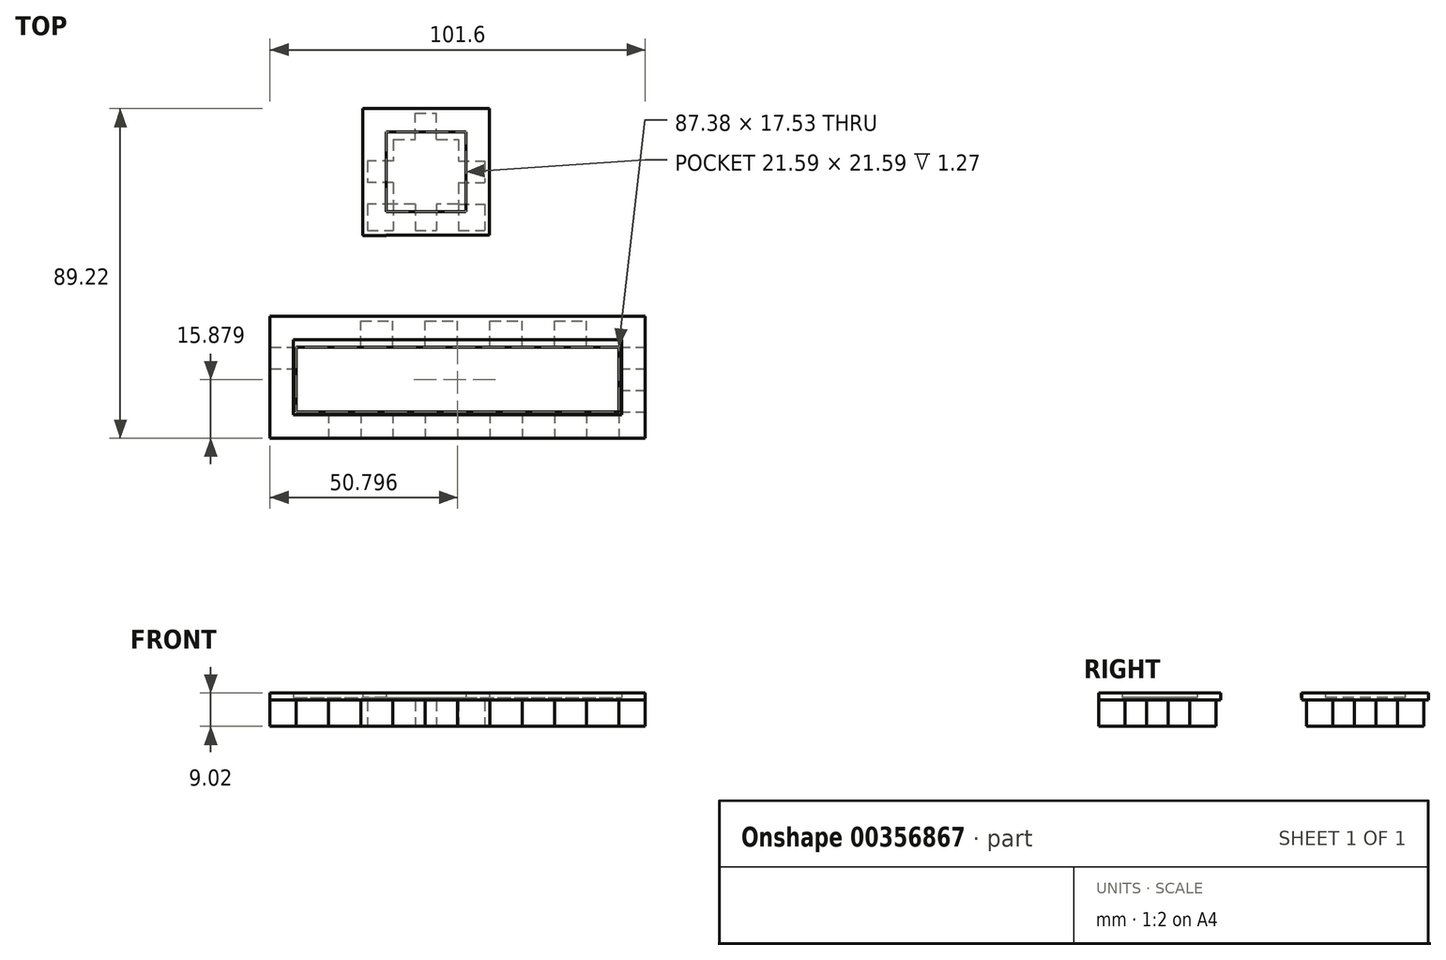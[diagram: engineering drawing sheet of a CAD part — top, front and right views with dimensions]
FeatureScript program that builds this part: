
annotation { "Feature Type Name" : "Feature", "Feature Type Description" : "" }
export const myFeature = defineFeature(function(context is Context, id is Id, definition is map)
    precondition{}
    {
        {
            var Q0;
            Q0=qCreatedBy(makeId("Top.planeOp"),FACE);
            var sketch = newSketch(context, id + "F0", { "sketchPlane" : qUnion([Q0])});
            skLineSegment(sketch, "E0.bottom", {"start": v(-52.12, 11.37) * mm, "end": v(49.48, 11.37) * mm});
            skLineSegment(sketch, "E0.top", {"start": v(-52.12, -20.38) * mm, "end": v(49.48, -20.38) * mm});
            skLineSegment(sketch, "E0.left", {"start": v(-52.12, 11.37) * mm, "end": v(-52.12, -20.38) * mm});
            skLineSegment(sketch, "E0.right", {"start": v(49.48, 11.37) * mm, "end": v(49.48, -20.38) * mm});
            skLineSegment(sketch, "E1.bottom", {"start": v(-52.12, 11.37) * mm, "end": v(-45.01, 11.37) * mm});
            skLineSegment(sketch, "E1.top", {"start": v(-52.12, 4.26) * mm, "end": v(-45.01, 4.26) * mm});
            skLineSegment(sketch, "E1.left", {"start": v(-52.12, 11.37) * mm, "end": v(-52.12, 4.26) * mm});
            skLineSegment(sketch, "E1.right", {"start": v(-45.01, 11.37) * mm, "end": v(-45.01, 4.26) * mm});
            skLineSegment(sketch, "E2.bottom", {"start": v(-45.01, 11.37) * mm, "end": v(-36.27, 11.37) * mm});
            skLineSegment(sketch, "E2.top", {"start": v(-45.01, 4.26) * mm, "end": v(-36.27, 4.26) * mm});
            skLineSegment(sketch, "E2.right", {"start": v(-36.27, 11.37) * mm, "end": v(-36.27, 4.26) * mm});
            skLineSegment(sketch, "E3.bottom", {"start": v(-36.27, 4.26) * mm, "end": v(-27.54, 4.26) * mm});
            skLineSegment(sketch, "E3.top", {"start": v(-36.27, 11.37) * mm, "end": v(-27.54, 11.37) * mm});
            skLineSegment(sketch, "E3.left", {"start": v(-36.27, 4.26) * mm, "end": v(-36.27, 11.37) * mm});
            skLineSegment(sketch, "E3.right", {"start": v(-27.54, 4.26) * mm, "end": v(-27.54, 11.37) * mm});
            skLineSegment(sketch, "E4.bottom", {"start": v(-27.54, 4.26) * mm, "end": v(-18.8, 4.26) * mm});
            skLineSegment(sketch, "E4.top", {"start": v(-27.54, 11.37) * mm, "end": v(-18.8, 11.37) * mm});
            skLineSegment(sketch, "E4.right", {"start": v(-18.8, 4.26) * mm, "end": v(-18.8, 11.37) * mm});
            skLineSegment(sketch, "E5.bottom", {"start": v(-18.8, 4.26) * mm, "end": v(-10.06, 4.26) * mm});
            skLineSegment(sketch, "E5.top", {"start": v(-18.8, 11.37) * mm, "end": v(-10.06, 11.37) * mm});
            skLineSegment(sketch, "E5.right", {"start": v(-10.06, 4.26) * mm, "end": v(-10.06, 11.37) * mm});
            skLineSegment(sketch, "E6.bottom", {"start": v(-10.06, 4.26) * mm, "end": v(-10.06, 4.26) * mm});
            skLineSegment(sketch, "E6.top", {"start": v(-10.06, 11.37) * mm, "end": v(-10.06, 11.37) * mm});
            skLineSegment(sketch, "E7.bottom", {"start": v(-10.06, 4.26) * mm, "end": v(-1.32, 4.26) * mm});
            skLineSegment(sketch, "E7.top", {"start": v(-10.06, 11.37) * mm, "end": v(-1.32, 11.37) * mm});
            skLineSegment(sketch, "E7.right", {"start": v(-1.32, 4.26) * mm, "end": v(-1.32, 11.37) * mm});
            skLineSegment(sketch, "E8.bottom", {"start": v(-1.32, 4.26) * mm, "end": v(7.41, 4.26) * mm});
            skLineSegment(sketch, "E8.top", {"start": v(-1.32, 11.37) * mm, "end": v(7.41, 11.37) * mm});
            skLineSegment(sketch, "E8.right", {"start": v(7.41, 4.26) * mm, "end": v(7.41, 11.37) * mm});
            skLineSegment(sketch, "E9.bottom", {"start": v(7.41, 4.26) * mm, "end": v(16.15, 4.26) * mm});
            skLineSegment(sketch, "E9.top", {"start": v(7.41, 11.37) * mm, "end": v(16.15, 11.37) * mm});
            skLineSegment(sketch, "E9.right", {"start": v(16.15, 4.26) * mm, "end": v(16.15, 11.37) * mm});
            skLineSegment(sketch, "E10.bottom", {"start": v(16.15, 4.26) * mm, "end": v(24.89, 4.26) * mm});
            skLineSegment(sketch, "E10.top", {"start": v(16.15, 11.37) * mm, "end": v(24.89, 11.37) * mm});
            skLineSegment(sketch, "E10.right", {"start": v(24.89, 4.26) * mm, "end": v(24.89, 11.37) * mm});
            skLineSegment(sketch, "E11.bottom", {"start": v(24.89, 4.26) * mm, "end": v(24.89, 4.26) * mm});
            skLineSegment(sketch, "E11.top", {"start": v(24.89, 11.37) * mm, "end": v(24.89, 11.37) * mm});
            skLineSegment(sketch, "E12.bottom", {"start": v(24.89, 4.26) * mm, "end": v(33.63, 4.26) * mm});
            skLineSegment(sketch, "E12.top", {"start": v(24.89, 11.37) * mm, "end": v(33.63, 11.37) * mm});
            skLineSegment(sketch, "E12.right", {"start": v(33.63, 4.26) * mm, "end": v(33.63, 11.37) * mm});
            skLineSegment(sketch, "E13.bottom", {"start": v(33.63, 4.26) * mm, "end": v(42.36, 4.26) * mm});
            skLineSegment(sketch, "E13.top", {"start": v(33.63, 11.37) * mm, "end": v(42.36, 11.37) * mm});
            skLineSegment(sketch, "E13.right", {"start": v(42.36, 4.26) * mm, "end": v(42.36, 11.37) * mm});
            skLineSegment(sketch, "E14.bottom", {"start": v(42.36, 4.26) * mm, "end": v(49.48, 4.26) * mm});
            skLineSegment(sketch, "E14.top", {"start": v(42.36, 11.37) * mm, "end": v(49.48, 11.37) * mm});
            skLineSegment(sketch, "E14.right", {"start": v(49.48, 4.26) * mm, "end": v(49.48, 11.37) * mm});
            skLineSegment(sketch, "E15.bottom", {"start": v(-52.12, -20.38) * mm, "end": v(-45.01, -20.38) * mm});
            skLineSegment(sketch, "E15.top", {"start": v(-52.12, -13.26) * mm, "end": v(-45.01, -13.26) * mm});
            skLineSegment(sketch, "E15.left", {"start": v(-52.12, -20.38) * mm, "end": v(-52.12, -13.26) * mm});
            skLineSegment(sketch, "E15.right", {"start": v(-45.01, -20.38) * mm, "end": v(-45.01, -13.26) * mm});
            skLineSegment(sketch, "E16.bottom", {"start": v(-45.01, -13.26) * mm, "end": v(-45.01, -13.26) * mm});
            skLineSegment(sketch, "E16.top", {"start": v(-45.01, -20.38) * mm, "end": v(-45.01, -20.38) * mm});
            skLineSegment(sketch, "E16.left", {"start": v(-45.01, -13.26) * mm, "end": v(-45.01, -20.38) * mm});
            skLineSegment(sketch, "E16.right", {"start": v(-45.01, -13.26) * mm, "end": v(-45.01, -20.38) * mm});
            skLineSegment(sketch, "E17.bottom", {"start": v(-45.01, -13.26) * mm, "end": v(-36.27, -13.26) * mm});
            skLineSegment(sketch, "E17.top", {"start": v(-45.01, -20.38) * mm, "end": v(-36.27, -20.38) * mm});
            skLineSegment(sketch, "E17.right", {"start": v(-36.27, -13.26) * mm, "end": v(-36.27, -20.38) * mm});
            skLineSegment(sketch, "E18.bottom", {"start": v(-36.27, -13.26) * mm, "end": v(-36.27, -13.26) * mm});
            skLineSegment(sketch, "E18.top", {"start": v(-36.27, -20.38) * mm, "end": v(-36.27, -20.38) * mm});
            skLineSegment(sketch, "E19.bottom", {"start": v(-36.27, -13.26) * mm, "end": v(-27.54, -13.26) * mm});
            skLineSegment(sketch, "E19.top", {"start": v(-36.27, -20.38) * mm, "end": v(-27.54, -20.38) * mm});
            skLineSegment(sketch, "E19.right", {"start": v(-27.54, -13.26) * mm, "end": v(-27.54, -20.38) * mm});
            skLineSegment(sketch, "E20.bottom", {"start": v(-27.54, -13.26) * mm, "end": v(-18.8, -13.26) * mm});
            skLineSegment(sketch, "E20.top", {"start": v(-27.54, -20.38) * mm, "end": v(-18.8, -20.38) * mm});
            skLineSegment(sketch, "E20.right", {"start": v(-18.8, -13.26) * mm, "end": v(-18.8, -20.38) * mm});
            skLineSegment(sketch, "E21.bottom", {"start": v(-18.8, -13.26) * mm, "end": v(-10.06, -13.26) * mm});
            skLineSegment(sketch, "E21.top", {"start": v(-18.8, -20.38) * mm, "end": v(-10.06, -20.38) * mm});
            skLineSegment(sketch, "E21.right", {"start": v(-10.06, -13.26) * mm, "end": v(-10.06, -20.38) * mm});
            skLineSegment(sketch, "E22.bottom", {"start": v(-10.06, -13.26) * mm, "end": v(-1.32, -13.26) * mm});
            skLineSegment(sketch, "E22.top", {"start": v(-10.06, -20.38) * mm, "end": v(-1.32, -20.38) * mm});
            skLineSegment(sketch, "E22.right", {"start": v(-1.32, -13.26) * mm, "end": v(-1.32, -20.38) * mm});
            skLineSegment(sketch, "E23.bottom", {"start": v(-1.32, -13.26) * mm, "end": v(7.41, -13.26) * mm});
            skLineSegment(sketch, "E23.top", {"start": v(-1.32, -20.38) * mm, "end": v(7.41, -20.38) * mm});
            skLineSegment(sketch, "E23.right", {"start": v(7.41, -13.26) * mm, "end": v(7.41, -20.38) * mm});
            skLineSegment(sketch, "E24.bottom", {"start": v(7.41, -13.26) * mm, "end": v(16.15, -13.26) * mm});
            skLineSegment(sketch, "E24.top", {"start": v(7.41, -20.38) * mm, "end": v(16.15, -20.38) * mm});
            skLineSegment(sketch, "E24.right", {"start": v(16.15, -13.26) * mm, "end": v(16.15, -20.38) * mm});
            skLineSegment(sketch, "E25.bottom", {"start": v(16.15, -13.26) * mm, "end": v(24.89, -13.26) * mm});
            skLineSegment(sketch, "E25.top", {"start": v(16.15, -20.38) * mm, "end": v(24.89, -20.38) * mm});
            skLineSegment(sketch, "E25.right", {"start": v(24.89, -13.26) * mm, "end": v(24.89, -20.38) * mm});
            skLineSegment(sketch, "E26.bottom", {"start": v(24.89, -13.26) * mm, "end": v(33.63, -13.26) * mm});
            skLineSegment(sketch, "E26.top", {"start": v(24.89, -20.38) * mm, "end": v(33.63, -20.38) * mm});
            skLineSegment(sketch, "E26.right", {"start": v(33.63, -13.26) * mm, "end": v(33.63, -20.38) * mm});
            skLineSegment(sketch, "E27.bottom", {"start": v(33.63, -13.26) * mm, "end": v(42.36, -13.26) * mm});
            skLineSegment(sketch, "E27.top", {"start": v(33.63, -20.38) * mm, "end": v(42.36, -20.38) * mm});
            skLineSegment(sketch, "E27.right", {"start": v(42.36, -13.26) * mm, "end": v(42.36, -20.38) * mm});
            skLineSegment(sketch, "E28.bottom", {"start": v(42.36, -13.26) * mm, "end": v(49.48, -13.26) * mm});
            skLineSegment(sketch, "E28.top", {"start": v(42.36, -20.38) * mm, "end": v(49.48, -20.38) * mm});
            skLineSegment(sketch, "E28.right", {"start": v(49.48, -13.26) * mm, "end": v(49.48, -20.38) * mm});
            skLineSegment(sketch, "E29.top", {"start": v(-52.12, -1.58) * mm, "end": v(-45.01, -1.58) * mm});
            skLineSegment(sketch, "E29.left", {"start": v(-52.12, 4.26) * mm, "end": v(-52.12, -1.58) * mm});
            skLineSegment(sketch, "E29.right", {"start": v(-45.01, 4.26) * mm, "end": v(-45.01, -1.58) * mm});
            skLineSegment(sketch, "E30.top", {"start": v(-52.12, -7.42) * mm, "end": v(-45.01, -7.42) * mm});
            skLineSegment(sketch, "E30.left", {"start": v(-52.12, -1.58) * mm, "end": v(-52.12, -7.42) * mm});
            skLineSegment(sketch, "E30.right", {"start": v(-45.01, -1.58) * mm, "end": v(-45.01, -7.42) * mm});
            skLineSegment(sketch, "E31.bottom", {"start": v(-45.01, -7.42) * mm, "end": v(-52.12, -7.42) * mm});
            skLineSegment(sketch, "E31.top", {"start": v(-45.01, -13.26) * mm, "end": v(-52.12, -13.26) * mm});
            skLineSegment(sketch, "E31.left", {"start": v(-45.01, -7.42) * mm, "end": v(-45.01, -13.26) * mm});
            skLineSegment(sketch, "E31.right", {"start": v(-52.12, -7.42) * mm, "end": v(-52.12, -13.26) * mm});
            skLineSegment(sketch, "E32.top", {"start": v(42.36, -1.58) * mm, "end": v(49.48, -1.58) * mm});
            skLineSegment(sketch, "E32.left", {"start": v(42.36, 4.26) * mm, "end": v(42.36, -1.58) * mm});
            skLineSegment(sketch, "E32.right", {"start": v(49.48, 4.26) * mm, "end": v(49.48, -1.58) * mm});
            skLineSegment(sketch, "E33.top", {"start": v(42.36, -7.42) * mm, "end": v(49.48, -7.42) * mm});
            skLineSegment(sketch, "E33.left", {"start": v(42.36, -1.58) * mm, "end": v(42.36, -7.42) * mm});
            skLineSegment(sketch, "E33.right", {"start": v(49.48, -1.58) * mm, "end": v(49.48, -7.42) * mm});
            skLineSegment(sketch, "E34.left", {"start": v(42.36, -7.42) * mm, "end": v(42.36, -13.26) * mm});
            skLineSegment(sketch, "E34.right", {"start": v(49.48, -7.42) * mm, "end": v(49.48, -13.26) * mm});
            skSolve(sketch);
        }
        {
            var Q0;
            Q0=makeQuery(id+"F0.imprint","IMPRINT",FACE,{"disambiguationData":[TD([[makeQuery(id+"F0.imprint","IMPRINT",EDGE,{"derivedFrom":sQuery(id+"F0.wireOp",EDGE,"E2.top")}),-1.0]])]});
            var Q1;
            Q1=makeQuery(id+"F0.imprint","IMPRINT",FACE,{"disambiguationData":[TD([[makeQuery(id+"F0.imprint","IMPRINT",EDGE,{"derivedFrom":sQuery(id+"F0.wireOp",EDGE,"E2.bottom")}),-1.0]])]});
            var Q2;
            Q2=makeQuery(id+"F0.imprint","IMPRINT",FACE,{"disambiguationData":[TD([[makeQuery(id+"F0.imprint","IMPRINT",EDGE,{"derivedFrom":sQuery(id+"F0.wireOp",EDGE,"E4.bottom")}),1.0]])]});
            var Q3;
            Q3=makeQuery(id+"F0.imprint","IMPRINT",FACE,{"disambiguationData":[TD([[makeQuery(id+"F0.imprint","IMPRINT",EDGE,{"derivedFrom":sQuery(id+"F0.wireOp",EDGE,"E7.bottom")}),1.0]])]});
            var Q4;
            Q4=makeQuery(id+"F0.imprint","IMPRINT",FACE,{"disambiguationData":[TD([[makeQuery(id+"F0.imprint","IMPRINT",EDGE,{"derivedFrom":sQuery(id+"F0.wireOp",EDGE,"E9.bottom")}),1.0]])]});
            var Q5;
            Q5=makeQuery(id+"F0.imprint","IMPRINT",FACE,{"disambiguationData":[TD([[makeQuery(id+"F0.imprint","IMPRINT",EDGE,{"derivedFrom":sQuery(id+"F0.wireOp",EDGE,"E12.bottom")}),1.0]])]});
            var Q6;
            Q6=makeQuery(id+"F0.imprint","IMPRINT",FACE,{"disambiguationData":[TD([[makeQuery(id+"F0.imprint","IMPRINT",EDGE,{"derivedFrom":sQuery(id+"F0.wireOp",EDGE,"E14.bottom")}),-1.0]])]});
            var Q7;
            Q7=makeQuery(id+"F0.imprint","IMPRINT",FACE,{"disambiguationData":[TD([[makeQuery(id+"F0.imprint","IMPRINT",EDGE,{"derivedFrom":sQuery(id+"F0.wireOp",EDGE,"E33.top")}),-1.0]])]});
            var Q8;
            Q8=makeQuery(id+"F0.imprint","IMPRINT",FACE,{"disambiguationData":[TD([[makeQuery(id+"F0.imprint","IMPRINT",EDGE,{"derivedFrom":sQuery(id+"F0.wireOp",EDGE,"E27.bottom")}),-1.0]])]});
            var Q9;
            Q9=makeQuery(id+"F0.imprint","IMPRINT",FACE,{"disambiguationData":[TD([[makeQuery(id+"F0.imprint","IMPRINT",EDGE,{"derivedFrom":sQuery(id+"F0.wireOp",EDGE,"E25.bottom")}),-1.0]])]});
            var Q10;
            Q10=makeQuery(id+"F0.imprint","IMPRINT",FACE,{"disambiguationData":[TD([[makeQuery(id+"F0.imprint","IMPRINT",EDGE,{"derivedFrom":sQuery(id+"F0.wireOp",EDGE,"E23.bottom")}),-1.0]])]});
            var Q11;
            Q11=makeQuery(id+"F0.imprint","IMPRINT",FACE,{"disambiguationData":[TD([[makeQuery(id+"F0.imprint","IMPRINT",EDGE,{"derivedFrom":sQuery(id+"F0.wireOp",EDGE,"E21.bottom")}),-1.0]])]});
            var Q12;
            Q12=makeQuery(id+"F0.imprint","IMPRINT",FACE,{"disambiguationData":[TD([[makeQuery(id+"F0.imprint","IMPRINT",EDGE,{"derivedFrom":sQuery(id+"F0.wireOp",EDGE,"E19.bottom")}),-1.0]])]});
            var Q13;
            Q13=makeQuery(id+"F0.imprint","IMPRINT",FACE,{"disambiguationData":[TD([[makeQuery(id+"F0.imprint","IMPRINT",EDGE,{"derivedFrom":sQuery(id+"F0.wireOp",EDGE,"E31.bottom")}),1.0]])]});
            var Q14;
            Q14=makeQuery(id+"F0.imprint","IMPRINT",FACE,{"disambiguationData":[TD([[makeQuery(id+"F0.imprint","IMPRINT",EDGE,{"derivedFrom":sQuery(id+"F0.wireOp",EDGE,"E1.top")}),-1.0]])]});
            extrude(context, id + "F1", {"entities" : qUnion([Q0, Q1, Q2, Q3, Q4, Q5, Q6, Q7, Q8, Q9, Q10, Q11, Q12, Q13, Q14]), "depth" : 7.11 * mm});
        }
        {
            var Q0;
            Q0=makeQuery(id+"F1.opExtrude","CAP_FACE",FACE,{"disambiguationData":[OSD([sQuery(id+"F0.wireOp",EDGE,"E2.bottom"),sQuery(id+"F0.wireOp",EDGE,"E1.right"),sQuery(id+"F0.wireOp",EDGE,"E3.bottom"),sQuery(id+"F0.wireOp",EDGE,"E3.left"),sQuery(id+"F0.wireOp",EDGE,"E4.top"),sQuery(id+"F0.wireOp",EDGE,"E3.right"),sQuery(id+"F0.wireOp",EDGE,"E5.bottom"),sQuery(id+"F0.wireOp",EDGE,"E4.right"),sQuery(id+"F0.wireOp",EDGE,"E6.top"),sQuery(id+"F0.wireOp",EDGE,"E5.right"),sQuery(id+"F0.wireOp",EDGE,"E7.bottom"),sQuery(id+"F0.wireOp",EDGE,"E5.right"),sQuery(id+"F0.wireOp",EDGE,"E8.top"),sQuery(id+"F0.wireOp",EDGE,"E7.right"),sQuery(id+"F0.wireOp",EDGE,"E9.bottom"),sQuery(id+"F0.wireOp",EDGE,"E8.right"),sQuery(id+"F0.wireOp",EDGE,"E10.top"),sQuery(id+"F0.wireOp",EDGE,"E9.right"),sQuery(id+"F0.wireOp",EDGE,"E11.bottom"),sQuery(id+"F0.wireOp",EDGE,"E10.right"),sQuery(id+"F0.wireOp",EDGE,"E12.top"),sQuery(id+"F0.wireOp",EDGE,"E10.right"),sQuery(id+"F0.wireOp",EDGE,"E13.bottom"),sQuery(id+"F0.wireOp",EDGE,"E12.right"),sQuery(id+"F0.wireOp",EDGE,"E16.bottom"),sQuery(id+"F0.wireOp",EDGE,"E17.top"),sQuery(id+"F0.wireOp",EDGE,"E16.left"),sQuery(id+"F0.wireOp",EDGE,"E18.bottom"),sQuery(id+"F0.wireOp",EDGE,"E17.right"),sQuery(id+"F0.wireOp",EDGE,"E19.top"),sQuery(id+"F0.wireOp",EDGE,"E17.right"),sQuery(id+"F0.wireOp",EDGE,"E20.bottom"),sQuery(id+"F0.wireOp",EDGE,"E19.right"),sQuery(id+"F0.wireOp",EDGE,"E21.top"),sQuery(id+"F0.wireOp",EDGE,"E20.right"),sQuery(id+"F0.wireOp",EDGE,"E22.bottom"),sQuery(id+"F0.wireOp",EDGE,"E21.right"),sQuery(id+"F0.wireOp",EDGE,"E23.top"),sQuery(id+"F0.wireOp",EDGE,"E22.right"),sQuery(id+"F0.wireOp",EDGE,"E24.bottom"),sQuery(id+"F0.wireOp",EDGE,"E23.right"),sQuery(id+"F0.wireOp",EDGE,"E25.top"),sQuery(id+"F0.wireOp",EDGE,"E24.right"),sQuery(id+"F0.wireOp",EDGE,"E26.bottom"),sQuery(id+"F0.wireOp",EDGE,"E25.right"),sQuery(id+"F0.wireOp",EDGE,"E27.top"),sQuery(id+"F0.wireOp",EDGE,"E26.right"),sQuery(id+"F0.wireOp",EDGE,"E27.right"),sQuery(id+"F0.wireOp",EDGE,"E1.top"),sQuery(id+"F0.wireOp",EDGE,"E29.left"),sQuery(id+"F0.wireOp",EDGE,"E29.top"),sQuery(id+"F0.wireOp",EDGE,"E30.right"),sQuery(id+"F0.wireOp",EDGE,"E31.bottom"),sQuery(id+"F0.wireOp",EDGE,"E31.top"),sQuery(id+"F0.wireOp",EDGE,"E31.right"),sQuery(id+"F0.wireOp",EDGE,"E14.bottom"),sQuery(id+"F0.wireOp",EDGE,"E32.right"),sQuery(id+"F0.wireOp",EDGE,"E32.top"),sQuery(id+"F0.wireOp",EDGE,"E33.left"),sQuery(id+"F0.wireOp",EDGE,"E33.top"),sQuery(id+"F0.wireOp",EDGE,"E28.bottom"),sQuery(id+"F0.wireOp",EDGE,"E34.right")])],"isStart":false});
            var sketch = newSketch(context, id + "F2", { "sketchPlane" : qUnion([Q0])});
            skLineSegment(sketch, "E35.bottom", {"start": v(-52.12, -20.38) * mm, "end": v(-45.01, -20.38) * mm});
            skLineSegment(sketch, "E35.top", {"start": v(-52.12, 12.64) * mm, "end": v(-45.01, 12.64) * mm});
            skLineSegment(sketch, "E35.left", {"start": v(-52.12, -20.38) * mm, "end": v(-52.12, 12.64) * mm});
            skLineSegment(sketch, "E35.right", {"start": v(-45.01, -20.38) * mm, "end": v(-45.01, 12.64) * mm});
            skLineSegment(sketch, "E36.bottom", {"start": v(-52.12, -20.38) * mm, "end": v(49.48, -20.38) * mm});
            skLineSegment(sketch, "E36.top", {"start": v(-52.12, -13.26) * mm, "end": v(49.48, -13.26) * mm});
            skLineSegment(sketch, "E36.left", {"start": v(-52.12, -20.38) * mm, "end": v(-52.12, -13.26) * mm});
            skLineSegment(sketch, "E36.right", {"start": v(49.48, -20.38) * mm, "end": v(49.48, -13.26) * mm});
            skPoint(sketch, "E37.oppositeSnap0", {"position": v(42.36, -4.5) * mm});
            skLineSegment(sketch, "E37.bottom", {"start": v(49.48, -20.38) * mm, "end": v(42.36, -20.38) * mm});
            skLineSegment(sketch, "E37.top", {"start": v(49.48, 12.64) * mm, "end": v(42.36, 12.64) * mm});
            skLineSegment(sketch, "E37.left", {"start": v(49.48, -20.38) * mm, "end": v(49.48, 12.64) * mm});
            skLineSegment(sketch, "E37.right", {"start": v(42.36, -20.38) * mm, "end": v(42.36, 12.64) * mm});
            skLineSegment(sketch, "E38.bottom", {"start": v(-52.12, 12.64) * mm, "end": v(49.48, 12.64) * mm});
            skLineSegment(sketch, "E38.top", {"start": v(-52.12, 4.26) * mm, "end": v(49.48, 4.26) * mm});
            skLineSegment(sketch, "E38.left", {"start": v(-52.12, 12.64) * mm, "end": v(-52.12, 4.26) * mm});
            skLineSegment(sketch, "E38.right", {"start": v(49.48, 12.64) * mm, "end": v(49.48, 4.26) * mm});
            skSolve(sketch);
        }
        {
            var Q0;
            Q0 = qSketchRegion(id + "F2", true);
            var Q1;
            {var subQ5=sQuery(id+"F2.wireOp",EDGE,"E36.top");var subQ10=sQuery(id+"F2.wireOp",EDGE,"E35.right");var subQ12=makeQuery(id+"F2.imprint","INTERSECT",VERTEX,{"derivedFrom":[makeQuery(id+"F1.opExtrude","CAP_EDGE",EDGE,{"disambiguationData":[OSD([sQuery(id+"F0.wireOp",EDGE,"E31.bottom")])],"isStart":false}),subQ10]});var subQ24=makeQuery(id+"F2.imprint","INTERSECT",VERTEX,{"derivedFrom":[subQ10,subQ5]});Q1=makeQuery(id+"F2.imprint","IMPRINT",FACE,{"disambiguationData":[TD([[makeQuery(id+"F2.imprint","IMPRINT",EDGE,{"disambiguationData":[TD([[subQ12,1.0],[subQ24,-1.0]])],"derivedFrom":subQ10}),-1.0]])]});}
            extrude(context, id + "F3", {"entities" : qUnion([Q0, Q1]), "depth" : 0.64 * mm});
        }
        {
            var Q0;
            Q0=qCreatedBy(makeId("Top.planeOp"),FACE);
            var sketch = newSketch(context, id + "F4", { "sketchPlane" : qUnion([Q0])});
            skLineSegment(sketch, "E39.bottom", {"start": v(-25.78, 67.57) * mm, "end": v(5.97, 67.57) * mm});
            skLineSegment(sketch, "E39.top", {"start": v(-25.78, 35.82) * mm, "end": v(5.97, 35.82) * mm});
            skLineSegment(sketch, "E39.left", {"start": v(-25.78, 67.57) * mm, "end": v(-25.78, 35.82) * mm});
            skLineSegment(sketch, "E39.right", {"start": v(5.97, 67.57) * mm, "end": v(5.97, 35.82) * mm});
            skLineSegment(sketch, "E40.bottom", {"start": v(-25.78, 67.57) * mm, "end": v(-18.67, 67.57) * mm});
            skLineSegment(sketch, "E40.top", {"start": v(-25.78, 60.46) * mm, "end": v(-18.67, 60.46) * mm});
            skLineSegment(sketch, "E40.left", {"start": v(-25.78, 67.57) * mm, "end": v(-25.78, 60.46) * mm});
            skLineSegment(sketch, "E40.right", {"start": v(-18.67, 67.57) * mm, "end": v(-18.67, 60.46) * mm});
            skLineSegment(sketch, "E41.bottom", {"start": v(-18.67, 60.46) * mm, "end": v(-12.83, 60.46) * mm});
            skLineSegment(sketch, "E41.top", {"start": v(-18.67, 67.57) * mm, "end": v(-12.83, 67.57) * mm});
            skLineSegment(sketch, "E41.left", {"start": v(-18.67, 60.46) * mm, "end": v(-18.67, 67.57) * mm});
            skLineSegment(sketch, "E41.right", {"start": v(-12.83, 60.46) * mm, "end": v(-12.83, 67.57) * mm});
            skLineSegment(sketch, "E42.bottom", {"start": v(-12.83, 60.46) * mm, "end": v(-6.98, 60.46) * mm});
            skLineSegment(sketch, "E42.top", {"start": v(-12.83, 67.57) * mm, "end": v(-6.98, 67.57) * mm});
            skLineSegment(sketch, "E42.right", {"start": v(-6.98, 60.46) * mm, "end": v(-6.98, 67.57) * mm});
            skLineSegment(sketch, "E43.bottom", {"start": v(-6.98, 60.46) * mm, "end": v(-1.14, 60.46) * mm});
            skLineSegment(sketch, "E43.top", {"start": v(-6.98, 67.57) * mm, "end": v(-1.14, 67.57) * mm});
            skLineSegment(sketch, "E43.right", {"start": v(-1.14, 60.46) * mm, "end": v(-1.14, 67.57) * mm});
            skLineSegment(sketch, "E44.bottom", {"start": v(-1.14, 60.46) * mm, "end": v(5.97, 60.46) * mm});
            skLineSegment(sketch, "E44.top", {"start": v(-1.14, 67.57) * mm, "end": v(5.97, 67.57) * mm});
            skLineSegment(sketch, "E44.right", {"start": v(5.97, 60.46) * mm, "end": v(5.97, 67.57) * mm});
            skLineSegment(sketch, "E45.bottom", {"start": v(-18.67, 60.46) * mm, "end": v(-25.78, 60.46) * mm});
            skLineSegment(sketch, "E45.top", {"start": v(-18.67, 54.62) * mm, "end": v(-25.78, 54.62) * mm});
            skLineSegment(sketch, "E45.left", {"start": v(-18.67, 60.46) * mm, "end": v(-18.67, 54.62) * mm});
            skLineSegment(sketch, "E45.right", {"start": v(-25.78, 60.46) * mm, "end": v(-25.78, 54.62) * mm});
            skLineSegment(sketch, "E46.top", {"start": v(-18.67, 48.78) * mm, "end": v(-25.78, 48.78) * mm});
            skLineSegment(sketch, "E46.left", {"start": v(-18.67, 54.62) * mm, "end": v(-18.67, 48.78) * mm});
            skLineSegment(sketch, "E46.right", {"start": v(-25.78, 54.62) * mm, "end": v(-25.78, 48.78) * mm});
            skLineSegment(sketch, "E47.top", {"start": v(-18.67, 42.94) * mm, "end": v(-25.78, 42.94) * mm});
            skLineSegment(sketch, "E47.left", {"start": v(-18.67, 48.78) * mm, "end": v(-18.67, 42.94) * mm});
            skLineSegment(sketch, "E47.right", {"start": v(-25.78, 48.78) * mm, "end": v(-25.78, 42.94) * mm});
            skLineSegment(sketch, "E48.top", {"start": v(-18.67, 35.82) * mm, "end": v(-25.78, 35.82) * mm});
            skLineSegment(sketch, "E48.left", {"start": v(-18.67, 42.94) * mm, "end": v(-18.67, 35.82) * mm});
            skLineSegment(sketch, "E48.right", {"start": v(-25.78, 42.94) * mm, "end": v(-25.78, 35.82) * mm});
            skLineSegment(sketch, "E49.top", {"start": v(-1.14, 54.62) * mm, "end": v(5.97, 54.62) * mm});
            skLineSegment(sketch, "E49.left", {"start": v(-1.14, 60.46) * mm, "end": v(-1.14, 54.62) * mm});
            skLineSegment(sketch, "E49.right", {"start": v(5.97, 60.46) * mm, "end": v(5.97, 54.62) * mm});
            skLineSegment(sketch, "E50.top", {"start": v(-1.14, 48.78) * mm, "end": v(5.97, 48.78) * mm});
            skLineSegment(sketch, "E50.left", {"start": v(-1.14, 54.62) * mm, "end": v(-1.14, 48.78) * mm});
            skLineSegment(sketch, "E50.right", {"start": v(5.97, 54.62) * mm, "end": v(5.97, 48.78) * mm});
            skLineSegment(sketch, "E51.top", {"start": v(-1.14, 42.94) * mm, "end": v(5.97, 42.94) * mm});
            skLineSegment(sketch, "E51.left", {"start": v(-1.14, 48.78) * mm, "end": v(-1.14, 42.94) * mm});
            skLineSegment(sketch, "E51.right", {"start": v(5.97, 48.78) * mm, "end": v(5.97, 42.94) * mm});
            skLineSegment(sketch, "E52.top", {"start": v(-1.14, 35.82) * mm, "end": v(5.97, 35.82) * mm});
            skLineSegment(sketch, "E52.left", {"start": v(-1.14, 42.94) * mm, "end": v(-1.14, 35.82) * mm});
            skLineSegment(sketch, "E52.right", {"start": v(5.97, 42.94) * mm, "end": v(5.97, 35.82) * mm});
            skLineSegment(sketch, "E53.bottom", {"start": v(-1.14, 42.94) * mm, "end": v(-6.98, 42.94) * mm});
            skLineSegment(sketch, "E53.top", {"start": v(-1.14, 35.82) * mm, "end": v(-6.98, 35.82) * mm});
            skLineSegment(sketch, "E53.right", {"start": v(-6.98, 42.94) * mm, "end": v(-6.98, 35.82) * mm});
            skLineSegment(sketch, "E54.bottom", {"start": v(-6.98, 42.94) * mm, "end": v(-12.83, 42.94) * mm});
            skLineSegment(sketch, "E54.top", {"start": v(-6.98, 35.82) * mm, "end": v(-12.83, 35.82) * mm});
            skLineSegment(sketch, "E54.right", {"start": v(-12.83, 42.94) * mm, "end": v(-12.83, 35.82) * mm});
            skLineSegment(sketch, "E55.bottom", {"start": v(-12.83, 42.94) * mm, "end": v(-18.67, 42.94) * mm});
            skLineSegment(sketch, "E55.top", {"start": v(-12.83, 35.82) * mm, "end": v(-18.67, 35.82) * mm});
            skSolve(sketch);
        }
        {
            var Q0;
            Q0=makeQuery(id+"F4.imprint","IMPRINT",FACE,{"disambiguationData":[TD([[makeQuery(id+"F4.imprint","IMPRINT",EDGE,{"derivedFrom":sQuery(id+"F4.wireOp",EDGE,"E40.bottom")}),-1.0]])]});
            var Q1;
            Q1=makeQuery(id+"F4.imprint","IMPRINT",FACE,{"disambiguationData":[TD([[makeQuery(id+"F4.imprint","IMPRINT",EDGE,{"derivedFrom":sQuery(id+"F4.wireOp",EDGE,"E42.bottom")}),1.0]])]});
            var Q2;
            Q2=makeQuery(id+"F4.imprint","IMPRINT",FACE,{"disambiguationData":[TD([[makeQuery(id+"F4.imprint","IMPRINT",EDGE,{"derivedFrom":sQuery(id+"F4.wireOp",EDGE,"E41.bottom")}),-1.0]])]});
            var Q3;
            Q3=makeQuery(id+"F4.imprint","IMPRINT",FACE,{"disambiguationData":[TD([[makeQuery(id+"F4.imprint","IMPRINT",EDGE,{"derivedFrom":sQuery(id+"F4.wireOp",EDGE,"E44.top")}),-1.0]])]});
            var Q4;
            Q4=makeQuery(id+"F4.imprint","IMPRINT",FACE,{"disambiguationData":[TD([[makeQuery(id+"F4.imprint","IMPRINT",EDGE,{"derivedFrom":sQuery(id+"F4.wireOp",EDGE,"E49.top")}),-1.0]])]});
            var Q5;
            Q5=makeQuery(id+"F4.imprint","IMPRINT",FACE,{"disambiguationData":[TD([[makeQuery(id+"F4.imprint","IMPRINT",EDGE,{"derivedFrom":sQuery(id+"F4.wireOp",EDGE,"E51.top")}),-1.0]])]});
            var Q6;
            Q6=makeQuery(id+"F4.imprint","IMPRINT",FACE,{"disambiguationData":[TD([[makeQuery(id+"F4.imprint","IMPRINT",EDGE,{"derivedFrom":sQuery(id+"F4.wireOp",EDGE,"E54.bottom")}),1.0]])]});
            var Q7;
            Q7=makeQuery(id+"F4.imprint","IMPRINT",FACE,{"disambiguationData":[TD([[makeQuery(id+"F4.imprint","IMPRINT",EDGE,{"derivedFrom":sQuery(id+"F4.wireOp",EDGE,"E47.top")}),1.0]])]});
            var Q8;
            Q8=makeQuery(id+"F4.imprint","IMPRINT",FACE,{"disambiguationData":[TD([[makeQuery(id+"F4.imprint","IMPRINT",EDGE,{"derivedFrom":sQuery(id+"F4.wireOp",EDGE,"E45.top")}),1.0]])]});
            extrude(context, id + "F5", {"entities" : qUnion([Q0, Q1, Q2, Q3, Q4, Q5, Q6, Q7, Q8]), "depth" : 7.11 * mm});
        }
        {
            var Q0;
            Q0=makeQuery(id+"F5.opExtrude","CAP_FACE",FACE,{"disambiguationData":[OSD([sQuery(id+"F4.wireOp",EDGE,"E41.bottom"),sQuery(id+"F4.wireOp",EDGE,"E42.top"),sQuery(id+"F4.wireOp",EDGE,"E41.right"),sQuery(id+"F4.wireOp",EDGE,"E43.bottom"),sQuery(id+"F4.wireOp",EDGE,"E42.right"),sQuery(id+"F4.wireOp",EDGE,"E45.left"),sQuery(id+"F4.wireOp",EDGE,"E45.top"),sQuery(id+"F4.wireOp",EDGE,"E46.right"),sQuery(id+"F4.wireOp",EDGE,"E46.top"),sQuery(id+"F4.wireOp",EDGE,"E47.left"),sQuery(id+"F4.wireOp",EDGE,"E49.left"),sQuery(id+"F4.wireOp",EDGE,"E49.top"),sQuery(id+"F4.wireOp",EDGE,"E50.right"),sQuery(id+"F4.wireOp",EDGE,"E50.top"),sQuery(id+"F4.wireOp",EDGE,"E51.left"),sQuery(id+"F4.wireOp",EDGE,"E53.bottom"),sQuery(id+"F4.wireOp",EDGE,"E54.top"),sQuery(id+"F4.wireOp",EDGE,"E53.right"),sQuery(id+"F4.wireOp",EDGE,"E55.bottom"),sQuery(id+"F4.wireOp",EDGE,"E54.right")])],"isStart":false});
            var sketch = newSketch(context, id + "F6", { "sketchPlane" : qUnion([Q0])});
            skLineSegment(sketch, "E56.bottom", {"start": v(-18.67, 34.55) * mm, "end": v(-27.05, 34.55) * mm});
            skLineSegment(sketch, "E56.top", {"start": v(-18.67, 68.84) * mm, "end": v(-27.05, 68.84) * mm});
            skLineSegment(sketch, "E56.left", {"start": v(-18.67, 34.55) * mm, "end": v(-18.67, 68.84) * mm});
            skLineSegment(sketch, "E56.right", {"start": v(-27.05, 34.55) * mm, "end": v(-27.05, 68.84) * mm});
            skPoint(sketch, "E57.oppositeSnap0", {"position": v(-4.06, 60.46) * mm});
            skLineSegment(sketch, "E57.bottom", {"start": v(-27.05, 68.84) * mm, "end": v(7.24, 68.84) * mm});
            skLineSegment(sketch, "E57.top", {"start": v(-27.05, 60.46) * mm, "end": v(7.24, 60.46) * mm});
            skLineSegment(sketch, "E57.left", {"start": v(-27.05, 68.84) * mm, "end": v(-27.05, 60.46) * mm});
            skLineSegment(sketch, "E57.right", {"start": v(7.24, 68.84) * mm, "end": v(7.24, 60.46) * mm});
            skLineSegment(sketch, "E58.bottom", {"start": v(7.24, 68.84) * mm, "end": v(-1.14, 68.84) * mm});
            skLineSegment(sketch, "E58.top", {"start": v(7.24, 34.55) * mm, "end": v(-1.14, 34.55) * mm});
            skLineSegment(sketch, "E58.left", {"start": v(7.24, 68.84) * mm, "end": v(7.24, 34.55) * mm});
            skLineSegment(sketch, "E58.right", {"start": v(-1.14, 68.84) * mm, "end": v(-1.14, 34.55) * mm});
            skLineSegment(sketch, "E59.bottom", {"start": v(7.24, 34.55) * mm, "end": v(-27.05, 34.55) * mm});
            skLineSegment(sketch, "E59.top", {"start": v(7.24, 42.94) * mm, "end": v(-27.05, 42.94) * mm});
            skLineSegment(sketch, "E59.left", {"start": v(7.24, 34.55) * mm, "end": v(7.24, 42.94) * mm});
            skLineSegment(sketch, "E59.right", {"start": v(-27.05, 34.55) * mm, "end": v(-27.05, 42.94) * mm});
            skSolve(sketch);
        }
        {
            var Q0;
            Q0 = qSketchRegion(id + "F6", true);
            var Q1;
            {var subQ4=sQuery(id+"F6.wireOp",EDGE,"E56.left");var subQ5=makeQuery(id+"F6.imprint","INTERSECT",VERTEX,{"derivedFrom":[makeQuery(id+"F5.opExtrude","CAP_EDGE",EDGE,{"disambiguationData":[OSD([sQuery(id+"F4.wireOp",EDGE,"E46.top")])],"isStart":false}),subQ4]});var subQ13=makeQuery(id+"F6.imprint","INTERSECT",VERTEX,{"derivedFrom":[makeQuery(id+"F5.opExtrude","CAP_EDGE",EDGE,{"disambiguationData":[OSD([sQuery(id+"F4.wireOp",EDGE,"E45.top")])],"isStart":false}),subQ4]});Q1=makeQuery(id+"F6.imprint","IMPRINT",FACE,{"disambiguationData":[TD([[makeQuery(id+"F6.imprint","IMPRINT",EDGE,{"disambiguationData":[TD([[subQ13,1.0],[subQ5,-1.0]])],"derivedFrom":subQ4}),-1.0]])]});}
            extrude(context, id + "F7", {"entities" : qUnion([Q0, Q1]), "depth" : 0.64 * mm});
        }
        {
            var Q0;
            Q0=makeQuery(id+"F3.opExtrude","CAP_FACE",FACE,{"disambiguationData":[OSD([sQuery(id+"F2.wireOp",EDGE,"E35.left"),sQuery(id+"F2.wireOp",EDGE,"E36.bottom"),sQuery(id+"F2.wireOp",EDGE,"E36.left"),sQuery(id+"F2.wireOp",EDGE,"E37.bottom"),sQuery(id+"F2.wireOp",EDGE,"E37.left"),sQuery(id+"F2.wireOp",EDGE,"E38.bottom"),sQuery(id+"F2.wireOp",EDGE,"E38.left"),sQuery(id+"F2.wireOp",EDGE,"E38.right")])],"isStart":false});
            var sketch = newSketch(context, id + "F8", { "sketchPlane" : qUnion([Q0])});
            skLineSegment(sketch, "E60.bottom", {"start": v(-52.12, 12.64) * mm, "end": v(49.48, 12.64) * mm});
            skLineSegment(sketch, "E60.top", {"start": v(-52.12, 6.3) * mm, "end": v(49.48, 6.3) * mm});
            skLineSegment(sketch, "E60.left", {"start": v(-52.12, 12.64) * mm, "end": v(-52.12, 6.3) * mm});
            skLineSegment(sketch, "E60.right", {"start": v(49.48, 12.64) * mm, "end": v(49.48, 6.3) * mm});
            skLineSegment(sketch, "E61.bottom", {"start": v(-52.12, 12.64) * mm, "end": v(-45.77, 12.64) * mm});
            skLineSegment(sketch, "E61.top", {"start": v(-52.12, -20.38) * mm, "end": v(-45.77, -20.38) * mm});
            skLineSegment(sketch, "E61.left", {"start": v(-52.12, 12.64) * mm, "end": v(-52.12, -20.38) * mm});
            skLineSegment(sketch, "E61.right", {"start": v(-45.77, 12.64) * mm, "end": v(-45.77, -20.38) * mm});
            skLineSegment(sketch, "E62.bottom", {"start": v(-52.12, -14.03) * mm, "end": v(49.48, -14.03) * mm});
            skLineSegment(sketch, "E62.top", {"start": v(-52.12, -20.38) * mm, "end": v(49.48, -20.38) * mm});
            skLineSegment(sketch, "E62.left", {"start": v(-52.12, -14.03) * mm, "end": v(-52.12, -20.38) * mm});
            skLineSegment(sketch, "E62.right", {"start": v(49.48, -14.03) * mm, "end": v(49.48, -20.38) * mm});
            skLineSegment(sketch, "E63.bottom", {"start": v(49.48, -20.38) * mm, "end": v(43.13, -20.38) * mm});
            skLineSegment(sketch, "E63.top", {"start": v(49.48, 12.64) * mm, "end": v(43.13, 12.64) * mm});
            skLineSegment(sketch, "E63.left", {"start": v(49.48, -20.38) * mm, "end": v(49.48, 12.64) * mm});
            skLineSegment(sketch, "E63.right", {"start": v(43.13, -20.38) * mm, "end": v(43.13, 12.64) * mm});
            skSolve(sketch);
        }
        {
            var Q0;
            Q0 = qSketchRegion(id + "F8", true);
            extrude(context, id + "F9", {"entities" : qUnion([Q0]), "operationType" : NewBodyOperationType.ADD, "depth" : 1.27 * mm});
        }
        {
            var Q0;
            Q0=makeQuery(id+"F7.opExtrude","CAP_FACE",FACE,{"disambiguationData":[OSD([sQuery(id+"F6.wireOp",EDGE,"E56.right"),sQuery(id+"F6.wireOp",EDGE,"E57.bottom"),sQuery(id+"F6.wireOp",EDGE,"E57.left"),sQuery(id+"F6.wireOp",EDGE,"E58.bottom"),sQuery(id+"F6.wireOp",EDGE,"E58.left"),sQuery(id+"F6.wireOp",EDGE,"E59.bottom"),sQuery(id+"F6.wireOp",EDGE,"E59.left"),sQuery(id+"F6.wireOp",EDGE,"E59.right")])],"isStart":false});
            var sketch = newSketch(context, id + "F10", { "sketchPlane" : qUnion([Q0])});
            skLineSegment(sketch, "E64.bottom", {"start": v(-27.05, 68.84) * mm, "end": v(7.24, 68.84) * mm});
            skLineSegment(sketch, "E64.top", {"start": v(-27.05, 62.5) * mm, "end": v(7.24, 62.5) * mm});
            skLineSegment(sketch, "E64.left", {"start": v(-27.05, 68.84) * mm, "end": v(-27.05, 62.5) * mm});
            skLineSegment(sketch, "E64.right", {"start": v(7.24, 68.84) * mm, "end": v(7.24, 62.5) * mm});
            skLineSegment(sketch, "E65.bottom", {"start": v(-27.05, 68.84) * mm, "end": v(-20.7, 68.84) * mm});
            skLineSegment(sketch, "E65.top", {"start": v(-27.05, 34.52) * mm, "end": v(-20.7, 34.52) * mm});
            skLineSegment(sketch, "E65.left", {"start": v(-27.05, 68.84) * mm, "end": v(-27.05, 34.52) * mm});
            skLineSegment(sketch, "E65.right", {"start": v(-20.7, 68.84) * mm, "end": v(-20.7, 34.52) * mm});
            skLineSegment(sketch, "E66.bottom", {"start": v(7.24, 68.84) * mm, "end": v(0.89, 68.84) * mm});
            skLineSegment(sketch, "E66.top", {"start": v(7.24, 34.55) * mm, "end": v(0.89, 34.55) * mm});
            skLineSegment(sketch, "E66.left", {"start": v(7.24, 68.84) * mm, "end": v(7.24, 34.55) * mm});
            skLineSegment(sketch, "E66.right", {"start": v(0.89, 68.84) * mm, "end": v(0.89, 34.55) * mm});
            skLineSegment(sketch, "E67.bottom", {"start": v(7.24, 34.55) * mm, "end": v(-27.05, 34.55) * mm});
            skLineSegment(sketch, "E67.top", {"start": v(7.24, 40.9) * mm, "end": v(-27.05, 40.9) * mm});
            skLineSegment(sketch, "E67.left", {"start": v(7.24, 34.55) * mm, "end": v(7.24, 40.9) * mm});
            skLineSegment(sketch, "E67.right", {"start": v(-27.05, 34.55) * mm, "end": v(-27.05, 40.9) * mm});
            skSolve(sketch);
        }
        {
            var Q0;
            Q0 = qSketchRegion(id + "F10", true);
            extrude(context, id + "F11", {"entities" : qUnion([Q0]), "operationType" : NewBodyOperationType.ADD, "depth" : 1.27 * mm});
        }
    });
